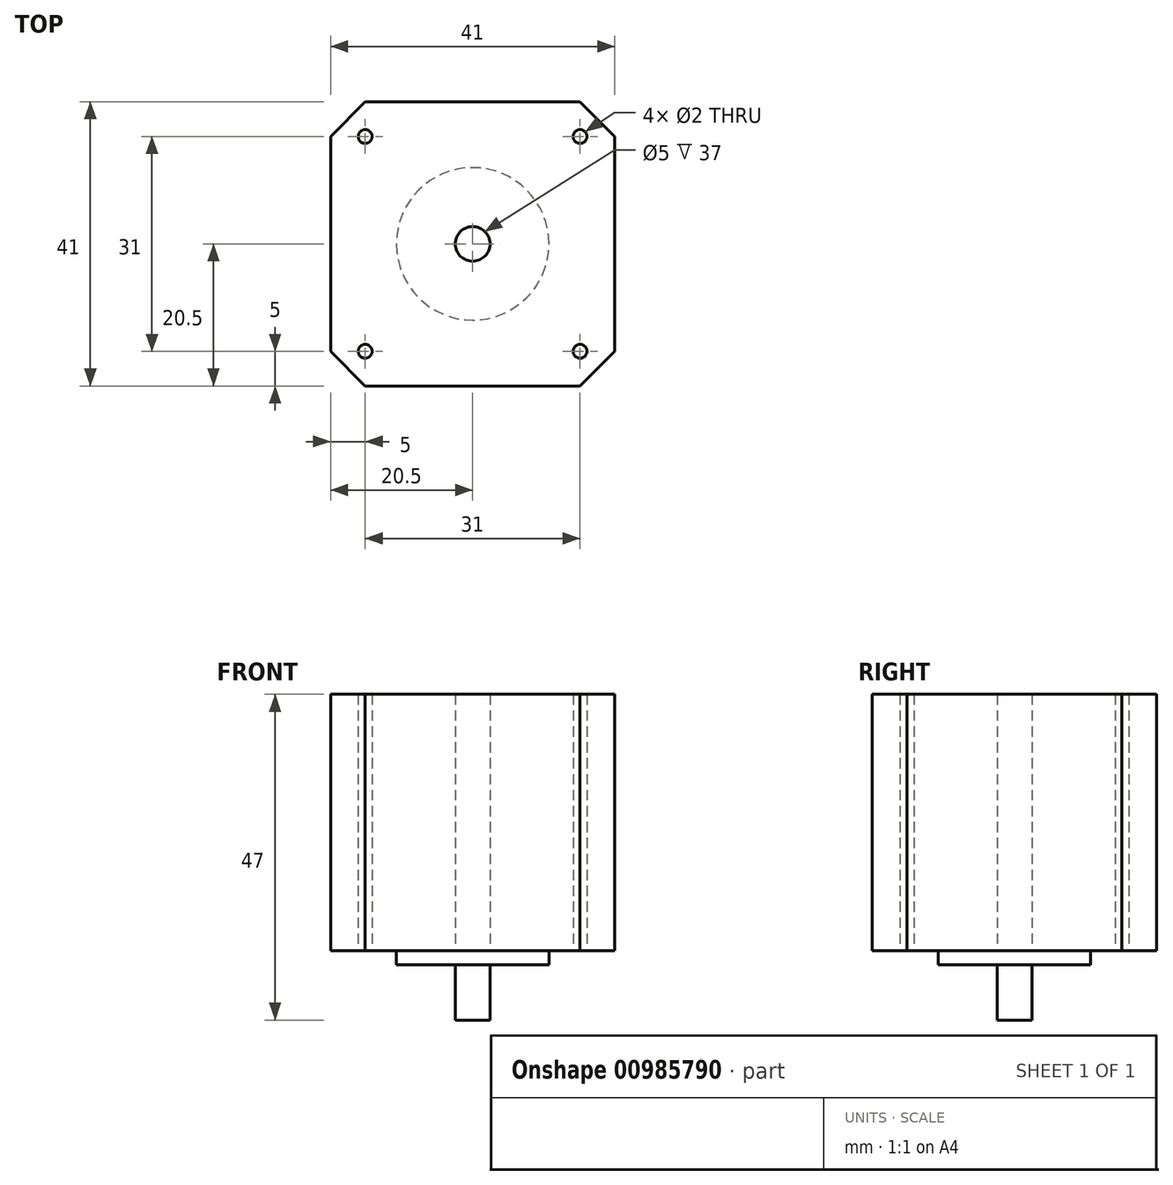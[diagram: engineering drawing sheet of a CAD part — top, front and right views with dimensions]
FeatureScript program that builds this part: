
annotation { "Feature Type Name" : "Feature", "Feature Type Description" : "" }
export const myFeature = defineFeature(function(context is Context, id is Id, definition is map)
    precondition{}
    {
        {
            var Q0;
            Q0=qCreatedBy(makeId("Top.planeOp"),FACE);
            var sketch = newSketch(context, id + "F0", { "sketchPlane" : qUnion([Q0])});
            skLineSegment(sketch, "E0.bottom", {"start": v(0, 0) * mm, "end": v(-41, 0) * mm});
            skLineSegment(sketch, "E0.top", {"start": v(0, 41) * mm, "end": v(-41, 41) * mm});
            skLineSegment(sketch, "E0.left", {"start": v(0, 0) * mm, "end": v(0, 41) * mm});
            skLineSegment(sketch, "E0.right", {"start": v(-41, 0) * mm, "end": v(-41, 41) * mm});
            skCircle(sketch, "E1", {"center": v(-5, 36) * mm, "radius": 1 * mm});
            skCircle(sketch, "E2", {"center": v(-5, 5) * mm, "radius": 1 * mm});
            skCircle(sketch, "E3", {"center": v(-36, 36) * mm, "radius": 1 * mm});
            skCircle(sketch, "E4", {"center": v(-36, 5) * mm, "radius": 1 * mm});
            skCircle(sketch, "E5", {"center": v(-20.5, 20.5) * mm, "radius": 11 * mm});
            skPoint(sketch, "E5.centerSnap0", {"position": v(-41, 20.5) * mm});
            skPoint(sketch, "E5.centerSnap1", {"position": v(-20.5, 0) * mm});
            skCircle(sketch, "E6", {"center": v(-20.5, 20.5) * mm, "radius": 2.5 * mm});
            skSolve(sketch);
        }
        {
            var Q0;
            Q0=makeQuery(id+"F0.imprint","IMPRINT",FACE,{"disambiguationData":[TD([[makeQuery(id+"F0.imprint","IMPRINT",EDGE,{"derivedFrom":sQuery(id+"F0.wireOp",EDGE,"E0.bottom")}),-1.0]])]});
            var Q1;
            Q1=makeQuery(id+"F0.imprint","IMPRINT",FACE,{"disambiguationData":[TD([[makeQuery(id+"F0.imprint","IMPRINT",EDGE,{"derivedFrom":sQuery(id+"F0.wireOp",EDGE,"E5")}),1.0]])]});
            extrude(context, id + "F1", {"entities" : qUnion([Q0, Q1]), "depth" : 37 * mm, "offsetDistance" : 25 * mm});
        }
        {
            var Q0;
            Q0=makeQuery(id+"F1.opExtrude","SWEPT_EDGE",EDGE,{"disambiguationData":[OSD([sQuery(id+"F0.wireOp",EDGE,"E0.top"),sQuery(id+"F0.wireOp",EDGE,"E0.left")])]});
            var Q1;
            Q1=makeQuery(id+"F1.opExtrude","SWEPT_EDGE",EDGE,{"disambiguationData":[OSD([sQuery(id+"F0.wireOp",EDGE,"E0.top"),sQuery(id+"F0.wireOp",EDGE,"E0.right")])]});
            var Q2;
            Q2=makeQuery(id+"F1.opExtrude","SWEPT_EDGE",EDGE,{"disambiguationData":[OSD([sQuery(id+"F0.wireOp",EDGE,"E0.bottom"),sQuery(id+"F0.wireOp",EDGE,"E0.left")])]});
            var Q3;
            Q3=makeQuery(id+"F1.opExtrude","SWEPT_EDGE",EDGE,{"disambiguationData":[OSD([sQuery(id+"F0.wireOp",EDGE,"E0.bottom"),sQuery(id+"F0.wireOp",EDGE,"E0.right")])]});
            chamfer(context, id + "F2", {"entities" : qUnion([Q0, Q1, Q2, Q3]), "width" : 5 * mm, "tangentPropagation" : true});
        }
        {
            var Q0;
            Q0=makeQuery(id+"F0.imprint","IMPRINT",FACE,{"disambiguationData":[TD([[makeQuery(id+"F0.imprint","IMPRINT",EDGE,{"derivedFrom":sQuery(id+"F0.wireOp",EDGE,"E5")}),1.0]])]});
            extrude(context, id + "F3", {"entities" : qUnion([Q0]), "operationType" : NewBodyOperationType.ADD, "oppositeDirection" : true, "depth" : 2 * mm, "offsetDistance" : 25 * mm});
        }
        {
            var Q0;
            Q0=makeQuery(id+"F0.imprint","IMPRINT",FACE,{"disambiguationData":[TD([[makeQuery(id+"F0.imprint","IMPRINT",EDGE,{"derivedFrom":sQuery(id+"F0.wireOp",EDGE,"E6")}),1.0]])]});
            extrude(context, id + "F4", {"entities" : qUnion([Q0]), "operationType" : NewBodyOperationType.ADD, "oppositeDirection" : true, "depth" : 10 * mm, "offsetDistance" : 25 * mm});
        }
    });
